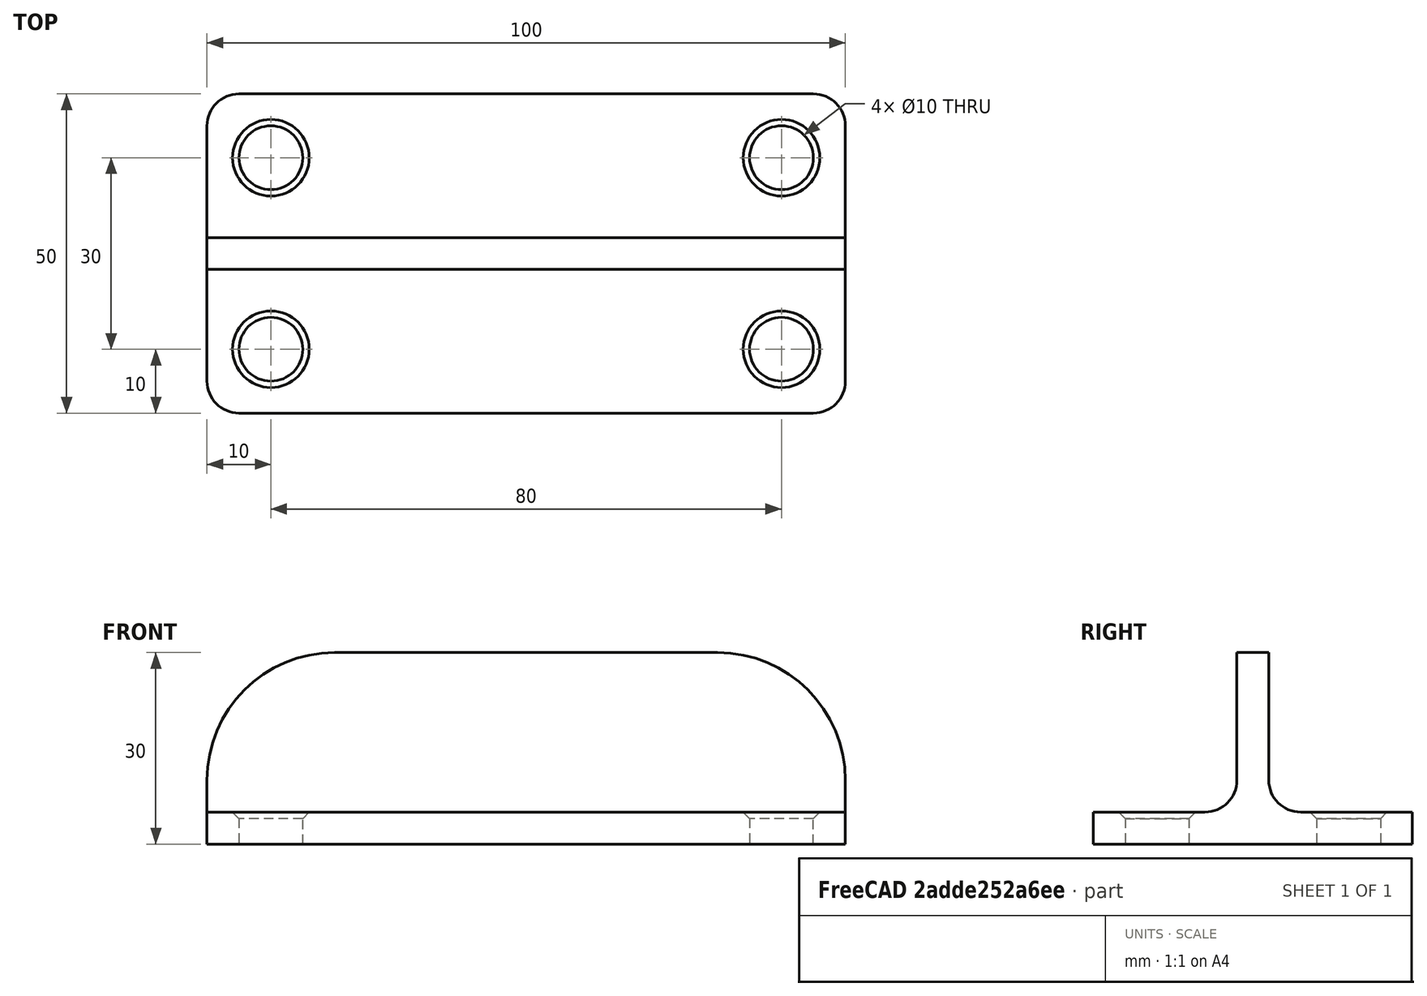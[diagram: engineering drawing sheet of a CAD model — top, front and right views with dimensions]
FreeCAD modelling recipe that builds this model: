
FCSTD DOCUMENT  (FreeCAD 0.21RUnknown)
Label: part3
License: All rights reserved
LicenseURL: https://en.wikipedia.org/wiki/All_rights_reserved
objects: TechDraw::DrawViewDimension×8, TechDraw::DrawProjGroupItem×3, Sketcher::SketchObject×2, PartDesign::Pad×2, PartDesign::Fillet×1, PartDesign::Chamfer×1, PartDesign::Body×1, TechDraw::DrawSVGTemplate×1, TechDraw::DrawViewPart×1, TechDraw::DrawProjGroup×1, TechDraw::DrawViewAnnotation×1, TechDraw::DrawPage×1
note: 22 computed .brp shape members not serialized (recipe doc carries the construction recipe); baked Part::Feature solids carry a one-line shape summary decoded from their .brp

FEATURE [Sketcher::SketchObject] Sketch
  FullyConstrained = true
  MapMode = 5
  Support = -> [XY_Plane]
  sketch-geometry (17):
    g0: LineSegment StartX=-50 StartY=20 StartZ=0 EndX=-50 EndY=-20 EndZ=0
    g1: LineSegment StartX=-45 StartY=-25 StartZ=0 EndX=45 EndY=-25 EndZ=0
    g2: LineSegment StartX=50 StartY=-20 StartZ=0 EndX=50 EndY=20 EndZ=0
    g3: LineSegment StartX=45 StartY=25 StartZ=0 EndX=-45 EndY=25 EndZ=0
    g4: GeomPoint X=0 Y=0 Z=0
    g5: Circle CenterX=-40 CenterY=15 CenterZ=0 NormalX=0 NormalY=0 NormalZ=1 AngleXU=0 Radius=5
    g6: Circle CenterX=40 CenterY=15 CenterZ=0 NormalX=0 NormalY=0 NormalZ=1 AngleXU=0 Radius=5
    g7: Circle CenterX=40 CenterY=-15 CenterZ=0 NormalX=0 NormalY=0 NormalZ=1 AngleXU=0 Radius=5
    g8: Circle CenterX=-40 CenterY=-15 CenterZ=0 NormalX=0 NormalY=0 NormalZ=1 AngleXU=0 Radius=5
    g9: ArcOfCircle CenterX=-45 CenterY=20 CenterZ=0 NormalX=0 NormalY=0 NormalZ=1 AngleXU=0 Radius=5 StartAngle=1.5708 EndAngle=3.14159
    g10: GeomPoint X=-50 Y=25 Z=0
    g11: ArcOfCircle CenterX=45 CenterY=20 CenterZ=0 NormalX=0 NormalY=0 NormalZ=1 AngleXU=0 Radius=5 StartAngle=2e-16 EndAngle=1.5708
    g12: GeomPoint X=50 Y=25 Z=0
    g13: ArcOfCircle CenterX=-45 CenterY=-20 CenterZ=0 NormalX=0 NormalY=0 NormalZ=1 AngleXU=0 Radius=5 StartAngle=3.14159 EndAngle=4.71239
    g14: GeomPoint X=-50 Y=-25 Z=0
    g15: ArcOfCircle CenterX=45 CenterY=-20 CenterZ=0 NormalX=0 NormalY=0 NormalZ=1 AngleXU=0 Radius=5 StartAngle=4.71239 EndAngle=6.28319
    g16: GeomPoint X=50 Y=-25 Z=0
  constraints (38):
    c: Horizontal(g1)
    c: Horizontal(g3)
    c: Vertical(g0)
    c: Vertical(g2)
    c: Symmetric(g16,g10,g4)
    c: Coincident(g4,g-1)
    c: DistanceX(g10,g12) = 100
    c: DistanceY(g16,g12) = 50
    c: Equal(g5,g6)
    c: Equal(g5,g7)
    c: Equal(g5,g8)
    c: Diameter(g5) = 10
    c: Symmetric(g5,g6,g-2)
    c: Symmetric(g5,g8,g-1)
    c: Vertical(g7,g6)
    c: Horizontal(g7,g8)
    c: DistanceY(g5,g10) = 10
    c: DistanceX(g10,g5) = 10
    c: PointOnObject(g10,g0)
    c: PointOnObject(g10,g3)
    c: Tangent(g0,g9) = -1.5708
    c: Tangent(g3,g9) = -1.5708
    c: PointOnObject(g12,g3)
    c: PointOnObject(g12,g2)
    c: Tangent(g3,g11) = -1.5708
    c: Tangent(g2,g11) = -1.5708
    c: Diameter(g9) = 10
    c: Equal(g9,g11)
    c: PointOnObject(g14,g0)
    c: PointOnObject(g14,g1)
    c: Tangent(g0,g13) = -1.5708
    c: Tangent(g1,g13) = -1.5708
    c: PointOnObject(g16,g1)
    c: PointOnObject(g16,g2)
    c: Tangent(g1,g15) = -1.5708
    c: Tangent(g2,g15) = -1.5708
    c: Equal(g13,g15)
    c: Equal(g15,g11)
FEATURE [PartDesign::Pad] Pad
  Direction = (0,0,1)
  Length = 5
  Length2 = 10
  Profile = -> Sketch
  ReferenceAxis = -> Sketch [N_Axis]
  Type = 0
FEATURE [Sketcher::SketchObject] Sketch001
  ExternalGeometry = -> [Pad]
  FullyConstrained = true
  MapMode = 5
  Placement = pos=(0,0,0) rot=(1,0,0;1.5708rad)
  Support = -> [XZ_Plane]
  sketch-geometry (8):
    g0: LineSegment StartX=-30 StartY=30 StartZ=0 EndX=30 EndY=30 EndZ=0
    g1: LineSegment StartX=50 StartY=10 StartZ=0 EndX=50 EndY=5 EndZ=0
    g2: LineSegment StartX=50 StartY=5 StartZ=0 EndX=-50 EndY=5 EndZ=0
    g3: LineSegment StartX=-50 StartY=5 StartZ=0 EndX=-50 EndY=10 EndZ=0
    g4: ArcOfCircle CenterX=-30 CenterY=10 CenterZ=0 NormalX=0 NormalY=0 NormalZ=1 AngleXU=0 Radius=20 StartAngle=1.5708 EndAngle=3.14159
    g5: GeomPoint X=-50 Y=30 Z=0
    g6: ArcOfCircle CenterX=30 CenterY=10 CenterZ=0 NormalX=0 NormalY=0 NormalZ=1 AngleXU=0 Radius=20 StartAngle=0 EndAngle=1.5708
    g7: GeomPoint X=50 Y=30 Z=0
  constraints (18):
    c: Coincident(g1,g2)
    c: Coincident(g2,g3)
    c: Horizontal(g0)
    c: Vertical(g1)
    c: Vertical(g3)
    c: Coincident(g1,g-3)
    c: Coincident(g2,g-4)
    c: DistanceY(g3,g5) = 25
    c: PointOnObject(g5,g3)
    c: PointOnObject(g5,g0)
    c: Tangent(g3,g4) = 1.5708
    c: Tangent(g0,g4) = 1.5708
    c: PointOnObject(g7,g0)
    c: PointOnObject(g7,g1)
    c: Tangent(g0,g6) = 1.5708
    c: Tangent(g1,g6) = 1.5708
    c: Equal(g4,g6)
    c: Diameter(g4) = 40
FEATURE [PartDesign::Pad] Pad001
  BaseFeature = -> Pad
  Direction = (0,-1,2e-16)
  Length = 5
  Length2 = 10
  Midplane = true
  Profile = -> Sketch001
  ReferenceAxis = -> Sketch001 [N_Axis]
  Type = 0
FEATURE [PartDesign::Fillet] Fillet
  Base = -> Pad001 [Edge31,Edge25]
  BaseFeature = -> Pad001
  Radius = 5
  SupportTransform = false
  UseAllEdges = false
FEATURE [PartDesign::Chamfer] Chamfer
  Angle = 45
  Base = -> Fillet [Edge38,Edge37,Edge14,Edge15]
  BaseFeature = -> Fillet
  ChamferType = 0
  FlipDirection = false
  Size = 1
  Size2 = 1
  SupportTransform = false
  UseAllEdges = false
FEATURE [PartDesign::Body] Body
  Group = -> [Sketch,Pad,Sketch001,Pad001,Fillet,Chamfer]
  Origin = -> Origin
  Tip = -> Chamfer
FEATURE [TechDraw::DrawSVGTemplate] Template
  Height = 297
  Orientation = 0
  Template = /nix/store/29d0l5zyj8xhlz06ml5gbz9jzk7y3hfr-freecad-0.21.2/share/Mod/TechDraw/Templates/A4_Portrait_blank.svg
  Width = 210
FEATURE [TechDraw::DrawViewPart] View
  Caption = 3D view
  CoarseView = false
  Direction = (0,0.707107,0.707107)
  Focus = 100
  HardHidden = false
  IsoCount = 0
  IsoHidden = false
  IsoVisible = false
  LockPosition = false
  Perspective = false
  Rotation = 12
  ScaleType = 0
  ScrubCount = 0
  SeamHidden = false
  SeamVisible = false
  SmoothHidden = false
  SmoothVisible = true
  Source = -> [Chamfer]
  X = 112.568
  XDirection = (0.783972,0.62079,0.00252448)
  Y = 189.927
FEATURE [TechDraw::DrawProjGroupItem] ProjItem  label="Top"
  Caption = Top view
  CoarseView = false
  Direction = (0,0,1)
  Focus = 100
  HardHidden = false
  IsoCount = 0
  IsoHidden = false
  IsoVisible = false
  LockPosition = true
  Perspective = false
  Rotation = 0
  RotationVector = (1,0,0)
  ScaleType = 2
  ScrubCount = 0
  SeamHidden = false
  SeamVisible = false
  SmoothHidden = false
  SmoothVisible = true
  Source = -> [Body]
  Type = 0
  X = 0
  XDirection = (1,0,0)
  Y = 0
FEATURE [TechDraw::DrawProjGroupItem] ProjItem001  label="Right"
  Caption = Left view
  CoarseView = false
  Direction = (1,0,1e-16)
  Focus = 100
  HardHidden = false
  IsoCount = 0
  IsoHidden = false
  IsoVisible = false
  LockPosition = false
  Perspective = false
  Rotation = -90
  RotationVector = (1,0,0)
  ScaleType = 2
  ScrubCount = 0
  SeamHidden = false
  SeamVisible = false
  SmoothHidden = false
  SmoothVisible = true
  Source = -> [Body]
  Type = 2
  X = -90
  XDirection = (1e-16,0,-1)
  Y = 0
FEATURE [TechDraw::DrawProjGroupItem] ProjItem002  label="Right001"
  Caption = Front view
  CoarseView = false
  Direction = (0,-1,0)
  Focus = 100
  HardHidden = false
  IsoCount = 0
  IsoHidden = false
  IsoVisible = false
  LockPosition = false
  Perspective = false
  Rotation = 0
  RotationVector = (1,0,0)
  ScaleType = 2
  ScrubCount = 0
  SeamHidden = false
  SeamVisible = false
  SmoothHidden = false
  SmoothVisible = true
  Source = -> [Body]
  Type = 5
  X = 0
  XDirection = (1,0,0)
  Y = 55
FEATURE [TechDraw::DrawProjGroup] ProjGroup
  Anchor = -> ProjItem
  AutoDistribute = true
  LockPosition = false
  ProjectionType = 0
  Rotation = 0
  ScaleType = 0
  Source = -> [Body]
  Views = -> [ProjItem,ProjItem001,ProjItem002]
  X = 126.784
  Y = 57.928
  spacingX = 15
  spacingY = 15
FEATURE [TechDraw::DrawViewDimension] Dimension
  AngleOverride = false
  Arbitrary = false
  ArbitraryTolerances = false
  EqualTolerance = true
  ExtensionAngle = 0
  FormatSpec = %.2w
  FormatSpecOverTolerance = %+.2w
  FormatSpecUnderTolerance = %+.2w
  Inverted = false
  LineAngle = 0
  LockPosition = false
  MeasureType = 1
  OverTolerance = 0
  References2D = -> [ProjItem]
  Rotation = 0
  ScaleType = 0
  TheoreticalExact = false
  Type = 2
  UnderTolerance = 0
  X = 60.9959
  Y = 2.29493
FEATURE [TechDraw::DrawViewDimension] Dimension001
  AngleOverride = false
  Arbitrary = false
  ArbitraryTolerances = false
  EqualTolerance = true
  ExtensionAngle = 0
  FormatSpec = %.2w
  FormatSpecOverTolerance = %+.2w
  FormatSpecUnderTolerance = %+.2w
  Inverted = false
  LineAngle = 0
  LockPosition = false
  MeasureType = 1
  OverTolerance = 0
  References2D = -> [ProjItem]
  Rotation = 0
  ScaleType = 0
  TheoreticalExact = false
  Type = 1
  UnderTolerance = 0
  X = 0.311498
  Y = -49.5635
FEATURE [TechDraw::DrawViewDimension] Dimension002
  AngleOverride = false
  Arbitrary = false
  ArbitraryTolerances = false
  EqualTolerance = true
  ExtensionAngle = 0
  FormatSpec = R%.2w
  FormatSpecOverTolerance = %+.2w
  FormatSpecUnderTolerance = %+.2w
  Inverted = false
  LineAngle = 0
  LockPosition = false
  MeasureType = 1
  OverTolerance = 0
  References2D = -> [ProjItem]
  Rotation = 0
  ScaleType = 0
  TheoreticalExact = false
  Type = 4
  UnderTolerance = 0
  X = 69.0376
  Y = -35.5408
FEATURE [TechDraw::DrawViewDimension] Dimension003
  AngleOverride = false
  Arbitrary = false
  ArbitraryTolerances = false
  EqualTolerance = true
  ExtensionAngle = 0
  FormatSpec = ⌀%.2w
  FormatSpecOverTolerance = %+.2w
  FormatSpecUnderTolerance = %+.2w
  Inverted = false
  LineAngle = 0
  LockPosition = false
  MeasureType = 1
  OverTolerance = 0
  References2D = -> [ProjItem]
  Rotation = 0
  ScaleType = 0
  TheoreticalExact = false
  Type = 5
  UnderTolerance = 0
  X = 72.6902
  Y = -15.4528
FEATURE [TechDraw::DrawViewDimension] Dimension004
  AngleOverride = false
  Arbitrary = false
  ArbitraryTolerances = false
  EqualTolerance = true
  ExtensionAngle = 0
  FormatSpec = R%.2w
  FormatSpecOverTolerance = %+.2w
  FormatSpecUnderTolerance = %+.2w
  Inverted = false
  LineAngle = 0
  LockPosition = false
  MeasureType = 1
  OverTolerance = 0
  References2D = -> [ProjItem002]
  Rotation = 0
  ScaleType = 0
  TheoreticalExact = false
  Type = 4
  UnderTolerance = 0
  X = -59.1554
  Y = 24.3865
FEATURE [TechDraw::DrawViewDimension] Dimension005
  AngleOverride = false
  Arbitrary = false
  ArbitraryTolerances = false
  EqualTolerance = true
  ExtensionAngle = 0
  FormatSpec = %.2w
  FormatSpecOverTolerance = %+.2w
  FormatSpecUnderTolerance = %+.2w
  Inverted = false
  LineAngle = 0
  LockPosition = false
  MeasureType = 1
  OverTolerance = 0
  References2D = -> [ProjItem002]
  Rotation = 0
  ScaleType = 0
  TheoreticalExact = false
  Type = 2
  UnderTolerance = 0
  X = -74.3865
  Y = -10
FEATURE [TechDraw::DrawViewDimension] Dimension006
  AngleOverride = false
  Arbitrary = false
  ArbitraryTolerances = false
  EqualTolerance = true
  ExtensionAngle = 0
  FormatSpec = %.2w
  FormatSpecOverTolerance = %+.2w
  FormatSpecUnderTolerance = %+.2w
  Inverted = false
  LineAngle = 0
  LockPosition = false
  MeasureType = 1
  OverTolerance = 0
  References2D = -> [ProjItem001]
  Rotation = 0
  ScaleType = 0
  TheoreticalExact = false
  Type = 1
  UnderTolerance = 0
  X = 0.241451
  Y = 31.5041
FEATURE [TechDraw::DrawViewDimension] Dimension007
  AngleOverride = false
  Arbitrary = false
  ArbitraryTolerances = false
  EqualTolerance = true
  ExtensionAngle = 0
  FormatSpec = %.2w
  FormatSpecOverTolerance = %+.2w
  FormatSpecUnderTolerance = %+.2w
  Inverted = false
  LineAngle = 0
  LockPosition = false
  MeasureType = 1
  OverTolerance = 0
  References2D = -> [ProjItem001]
  Rotation = 0
  ScaleType = 0
  TheoreticalExact = false
  Type = 2
  UnderTolerance = 0
  X = -15.1409
  Y = 6.69015
FEATURE [TechDraw::DrawViewAnnotation] Annotation
  Font = osifont
  LineSpace = 100
  LockPosition = false
  MaxWidth = -1
  Rotation = 0
  ScaleType = 0
  Text = My project
  TextSize = 5
  TextStyle = 0
  X = 153.86
  Y = 265.654
FEATURE [TechDraw::DrawPage] Page
  KeepUpdated = true
  NextBalloonIndex = 1
  ProjectionType = 0
  Template = -> Template
  Views = -> [View,ProjGroup,Dimension,Dimension001,Dimension002,Dimension003,Dimension004,Dimension005,Dimension006,Dimension007,Annotation]
